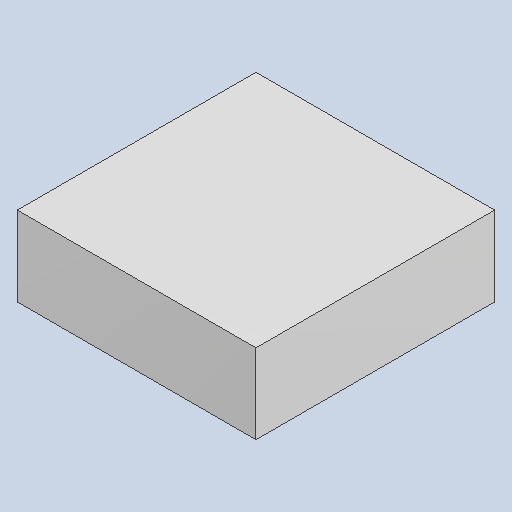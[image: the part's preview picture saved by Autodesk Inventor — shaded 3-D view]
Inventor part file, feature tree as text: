
AUTODESK INVENTOR PART (.ipt)
format: ipt  version: 2023.4 (Build 274418000, 418)  size: 79,872 bytes
history: native  units: mm
features: extrude x1
ambient origin geometry x8: Origin, YZ Plane, XZ Plane, XY Plane, X Axis, Y Axis, Z Axis, Center Point
bodies: Solid1 (feature_tree)
feature tree (1):
  extrude  "Extruded_10"  [1 undecoded]
note: 1 required parameter value undecoded (feature->parameter linkage not recoverable at this tier; creation-order binding heuristic only, values carry confidence <= 0.55)
